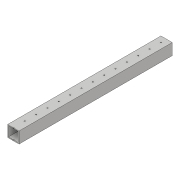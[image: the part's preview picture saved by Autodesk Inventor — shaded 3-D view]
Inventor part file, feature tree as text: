
AUTODESK INVENTOR PART (.ipt)
format: ipt  version: 2018 (Build 220112000, 112)  size: 119,296 bytes
history: native  units: in
note: dims shown in document units (in); Inventor stores cm internally (conversion verified against a paired STEP export)
features: sketch x2, extrude x1, hole x1
ambient origin geometry x8: Origin, YZ Plane, XZ Plane, XY Plane, X Axis, Y Axis, Z Axis, Center Point
bodies: Solid1 (feature_tree)
feature tree (4):
  extrude  "Extrusion1"  Depth=1.0in
  hole  "Hole1"  [1 undecoded]
  sketch  "Sketch1"  dims[d0=1.0in d1=1.0in]
  sketch  "Sketch2"  dims[d2=0.0625in d3=0.0625in d4=13.5in d5=0.0in d6=0.5in d7=0.5in d8=6.2992in d10=1.0in d11=0.3937in d13=1.0in d15=0.1in d16=0.75in d17=0.375in d18=0.25in d19=0.5635in d20=1.0in d21=0.8108in]
note: 1 required parameter value undecoded (feature->parameter linkage not recoverable at this tier; creation-order binding heuristic only, values carry confidence <= 0.55)
